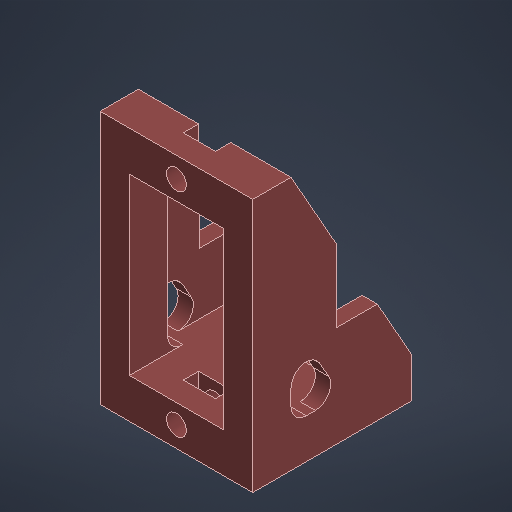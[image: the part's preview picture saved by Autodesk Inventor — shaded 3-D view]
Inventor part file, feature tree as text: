
AUTODESK INVENTOR PART (.ipt)
format: ipt  version: 2025.1 (Build 291241000, 241)  size: 495,104 bytes
history: native  units: in
note: dims shown in document units (in); Inventor stores cm internally (conversion verified against a paired STEP export)
features: extrude x6, sketch x5, plane x2, mirror x1, fillet x1
ambient origin geometry x8: Origin, YZ Plane, XZ Plane, XY Plane, X Axis, Y Axis, Z Axis, Center Point
bodies: Solid1 (feature_tree)
feature tree (15):
  sketch  "Sketch1"  dims[d0=0.1024in d1=1.0945in]
  extrude  "Extrusion1"  Depth=1.0945in
  extrude  "Extrusion2"  Depth=0.0984in
  extrude  "Extrusion3"  Depth=0.8976in
  extrude  "Extrusion4"  Depth=0.1063in
  sketch  "Sketch4"  dims[d11=0.1063in d12=0.1063in]
  plane  "Work Plane1"
  extrude  "Extrusion5"  Depth=0.1969in TaperAngle=0.0deg
  plane  "Work Plane3"
  mirror  "Mirror1"
  fillet  "Fillet1"  Radius=0.622in
  extrude  "Extrusion7"  Depth=0.0787in
  sketch  "Sketch2"  dims[d4=0.4843in d5=0.0984in]
  sketch  "Sketch3"  dims[d6=0.0984in d7=0.8976in]
  sketch  "Sketch5"  dims[d14=0.1506in d15=0.1969in d16=0.0in d17=0.622in d18=0.0in d19=0.0827in d20=0.0in d21=0.2093in d22=0.3268in d24=0.3937in d25=0.0in d26=0.1969in d27=0.0787in d28=0.0in d29=0.315in d30=-0.3406in d31=0.0787in d32=0.0in d33=0.315in d34=0.2362in d37=0.0787in d39=0.1654in d40=0.1181in d41=0.0787in d42=0.0in d43=0.0in]
